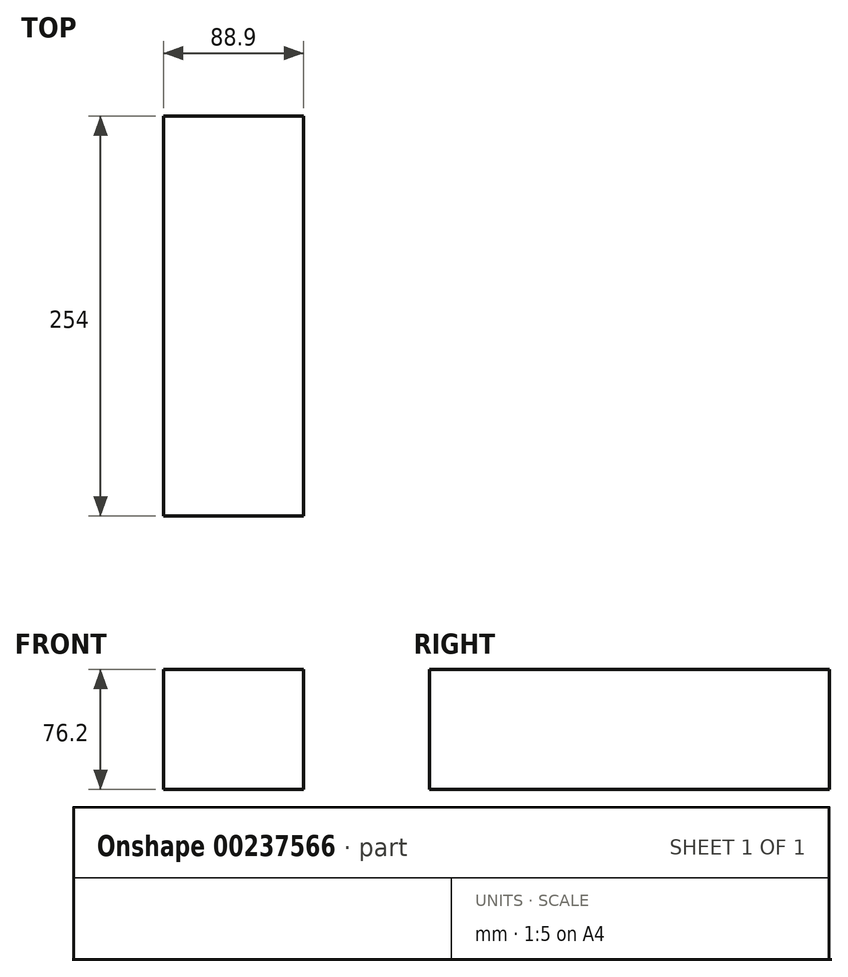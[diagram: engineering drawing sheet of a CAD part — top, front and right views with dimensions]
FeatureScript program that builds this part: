
annotation { "Feature Type Name" : "Feature", "Feature Type Description" : "" }
export const myFeature = defineFeature(function(context is Context, id is Id, definition is map)
    precondition{}
    {
        {
            var Q0;
            Q0=qCreatedBy(makeId("Top.planeOp"),FACE);
            var sketch = newSketch(context, id + "F0", { "sketchPlane" : qUnion([Q0])});
            skLineSegment(sketch, "E0.bottom", {"start": v(-231.84, 132.75) * mm, "end": v(-142.94, 132.75) * mm});
            skLineSegment(sketch, "E0.top", {"start": v(-231.84, -121.25) * mm, "end": v(-142.94, -121.25) * mm});
            skLineSegment(sketch, "E0.left", {"start": v(-231.84, 132.75) * mm, "end": v(-231.84, -121.25) * mm});
            skLineSegment(sketch, "E0.right", {"start": v(-142.94, 132.75) * mm, "end": v(-142.94, -121.25) * mm});
            skSolve(sketch);
        }
        {
            var Q0;
            Q0=makeQuery(id+"F0.imprint","IMPRINT",FACE,{"disambiguationData":[TD([[makeQuery(id+"F0.imprint","IMPRINT",EDGE,{"derivedFrom":sQuery(id+"F0.wireOp",EDGE,"E0.bottom")}),-1.0]])]});
            extrude(context, id + "F1", {"entities" : qUnion([Q0]), "depth" : 76.2 * mm});
        }
    });
